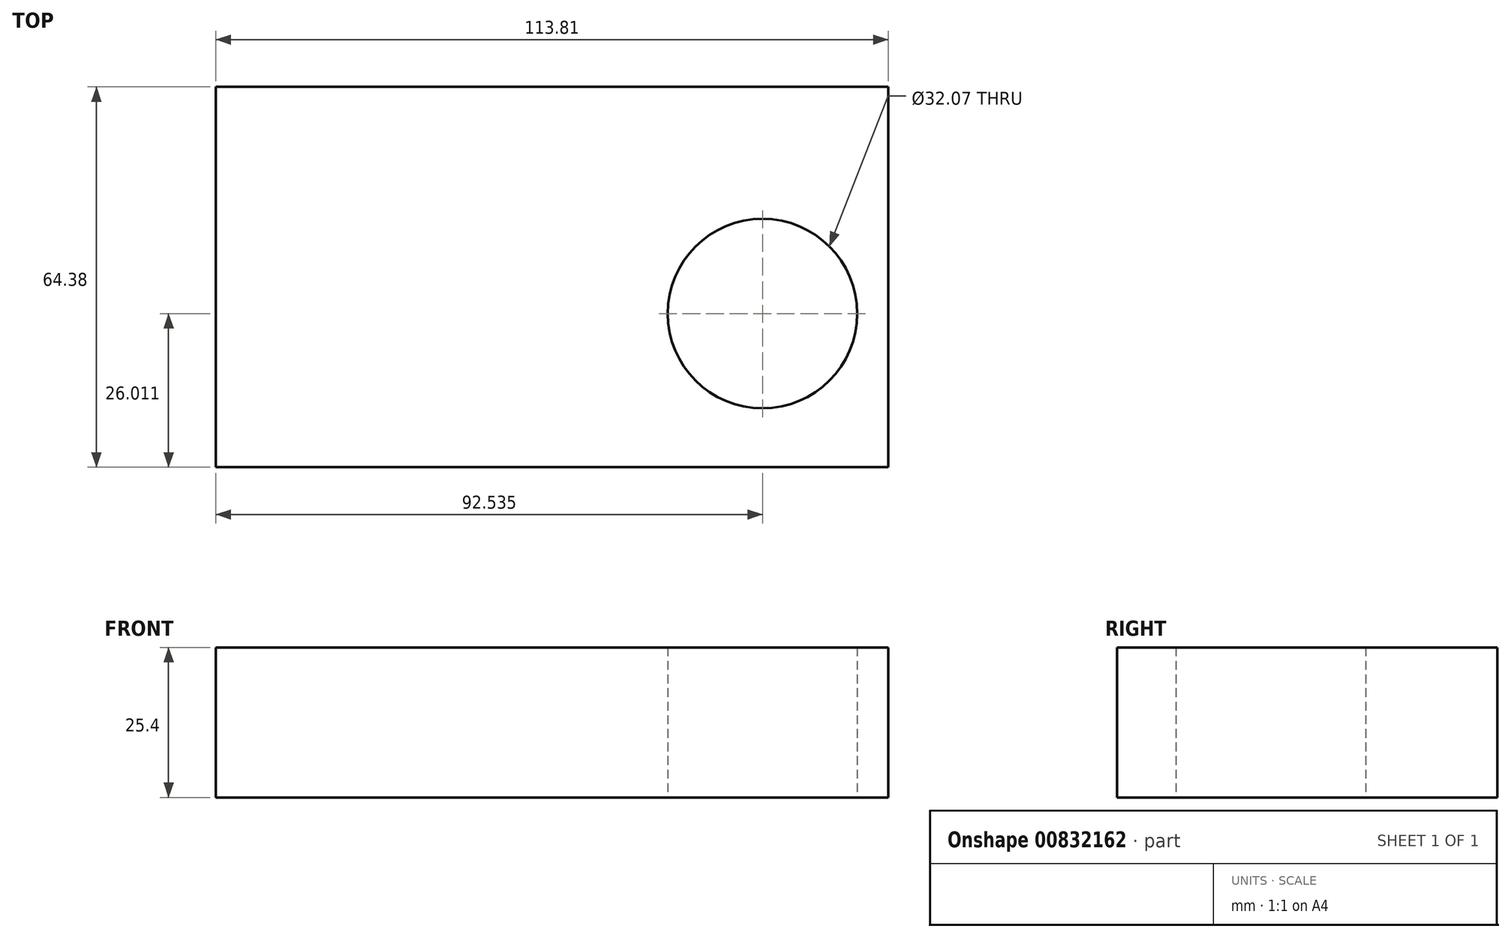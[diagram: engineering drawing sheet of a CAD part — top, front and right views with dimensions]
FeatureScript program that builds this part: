
annotation { "Feature Type Name" : "Feature", "Feature Type Description" : "" }
export const myFeature = defineFeature(function(context is Context, id is Id, definition is map)
    precondition{}
    {
        {
            var Q0;
            Q0=qCreatedBy(makeId("Top.planeOp"),FACE);
            var sketch = newSketch(context, id + "F0", { "sketchPlane" : qUnion([Q0])});
            skLineSegment(sketch, "E0.bottom", {"start": v(-46.27, 41.7) * mm, "end": v(67.54, 41.7) * mm});
            skLineSegment(sketch, "E0.top", {"start": v(-46.27, -22.68) * mm, "end": v(67.54, -22.68) * mm});
            skLineSegment(sketch, "E0.left", {"start": v(-46.27, 41.7) * mm, "end": v(-46.27, -22.68) * mm});
            skLineSegment(sketch, "E0.right", {"start": v(67.54, 41.7) * mm, "end": v(67.54, -22.68) * mm});
            skCircle(sketch, "E1", {"center": v(46.27, 3.33) * mm, "radius": 16.04 * mm});
            skSolve(sketch);
        }
        {
            var Q0;
            Q0 = qSketchRegion(id + "F0", true);
            extrude(context, id + "F1", {"entities" : qUnion([Q0]), "depth" : 25.4 * mm, "offsetDistance" : 25.4 * mm});
        }
    });
